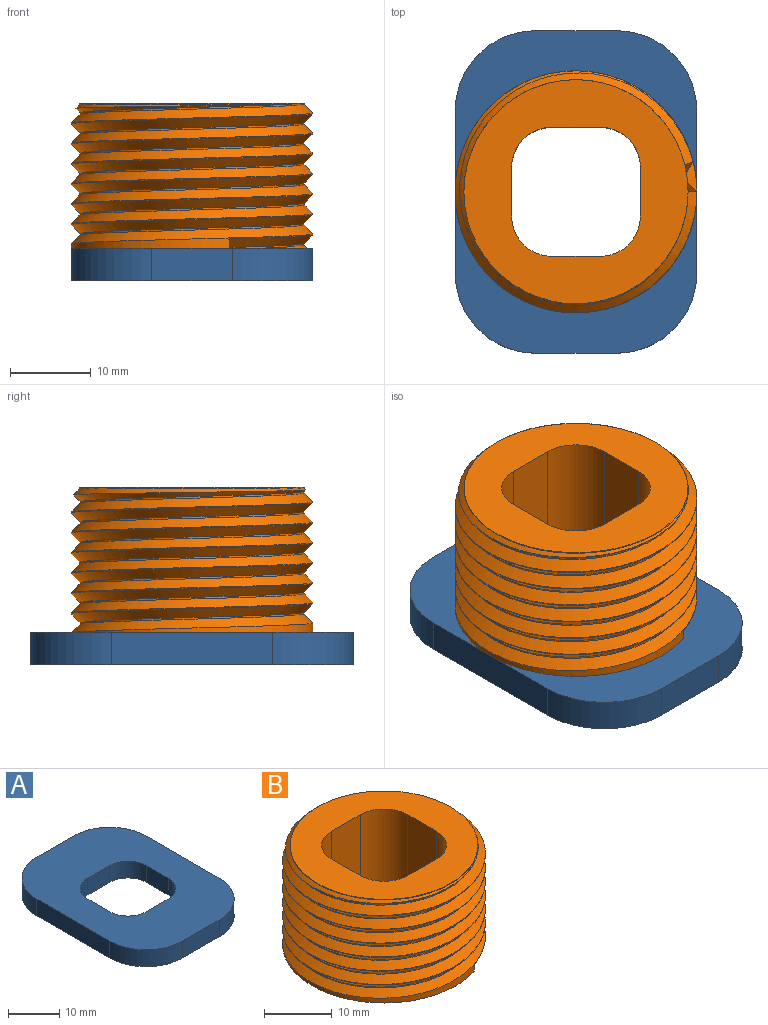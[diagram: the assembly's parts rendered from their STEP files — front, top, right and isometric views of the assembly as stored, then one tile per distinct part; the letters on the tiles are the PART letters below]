
ASSEMBLY  parts=2 mates=1
PART A: 18 faces, bbox 30x40x4 mm
  f0: plane 6x4mm, normal (1,0,0), area 24mm2, adj f4,f7,f8,f9
  f1: plane 6x4mm, normal (0,-1,0), area 24mm2, adj f4,f5,f8,f9
  f2: plane 6x4mm, normal (-1,0,0), area 24mm2, adj f5,f6,f8,f9
  f3: plane 6x4mm, normal (0,1,0), area 24mm2, adj f6,f7,f8,f9
  f4: cylinder r=5mm len=5mm, axis (0,0,-1), area 31.4mm2, adj f0,f1,f8,f9
  f5: cylinder r=5mm len=5mm, axis (0,0,1), area 31.4mm2, adj f1,f2,f8,f9
  f6: cylinder r=5mm len=5mm, axis (0,0,-1), area 31.4mm2, adj f2,f3,f8,f9
  f7: cylinder r=5mm len=5mm, axis (0,0,1), area 31.4mm2, adj f0,f3,f8,f9
  f8: plane 40x30mm, normal (0,0,1), area 879.6mm2, adj f0,f1,f2,f3,f4,f5,f6,f7
  f9: plane 40x30mm, normal (0,0,-1), area 879.6mm2, adj f0,f1,f2,f3,f4,f5,f6,f7
  f10: plane 20x4mm, normal (1,0,0), area 80mm2, adj f8,f9,f14,f17
  f11: plane 10x4mm, normal (0,1,0), area 40mm2, adj f8,f9,f14,f15
  f12: plane 20x4mm, normal (-1,0,0), area 80mm2, adj f8,f9,f15,f16
  f13: plane 10x4mm, normal (0,-1,0), area 40mm2, adj f8,f9,f16,f17
  f14: cylinder r=10mm len=10mm, axis (0,0,1), area 62.8mm2, adj f8,f9,f10,f11
  f15: cylinder r=10mm len=10mm, axis (0,0,-1), area 62.8mm2, adj f8,f9,f11,f12
  f16: cylinder r=10mm len=10mm, axis (0,0,1), area 62.8mm2, adj f8,f9,f12,f13
  f17: cylinder r=10mm len=10mm, axis (0,0,-1), area 62.8mm2, adj f8,f9,f10,f13
PART B: 17 faces, bbox 30.1x34.7x20.3 mm
  f0: cylinder r=15mm len=30mm, axis (0,0,-1), area -339.8mm2, adj f1,f3,f4,f6
  f1: bspline ~34.64x30.04mm, area 945.7mm2, adj f0,f4,f5,f16
  f2: plane 28.03x27.93mm, normal (0,0,1), area 372.5mm2, adj f5,f7,f8,f9,f10,f11,f12,f13
  f3: plane 29.98x29.35mm, normal (0,0,-1), area 446mm2, adj f0,f4,f5,f6,f7,f8,f9,f10
  f4: plane 1.21x1.06mm, normal (0.95,0.31,0.03), area 0.7mm2, adj f0,f1,f3,f5
  f5: bspline ~32.1x27.8mm, area 123.8mm2, adj f1,f2,f3,f4,f6,f15
  f6: bspline ~29.99x29.97mm, area 929.5mm2, adj f0,f3,f5,f16
  f7: plane 18x6mm, normal (0,-1,0), area 108mm2, adj f2,f3,f11,f14
  f8: plane 18x6mm, normal (1,0,0), area 108mm2, adj f2,f3,f11,f12
  f9: plane 18x6mm, normal (0,1,0), area 108mm2, adj f2,f3,f12,f13
  f10: plane 18x6mm, normal (-1,0,0), area 108mm2, adj f2,f3,f13,f14
  f11: cylinder r=5mm len=18mm, axis (0,0,1), area 141.4mm2, adj f2,f3,f7,f8
  f12: cylinder r=5mm len=18mm, axis (0,0,-1), area 141.4mm2, adj f2,f3,f8,f9
  f13: cylinder r=5mm len=18mm, axis (0,0,1), area 141.4mm2, adj f2,f3,f9,f10
  f14: cylinder r=5mm len=18mm, axis (0,0,-1), area 141.4mm2, adj f2,f3,f7,f10
  f15: revolved ~27.78x27.77mm, area 8.4mm2, adj f2,f5,f16
  f16: revolved ~29.98x29.96mm, area -66.6mm2, adj f1,f6,f15
PLACE A t=(15.73,35.19,-23.83)mm
PLACE B t=(15.73,35.19,30.17)mm
MATE fastened A.f8 <-> B.f0  axis (0,0,1) through (15.73,35.19,30.17)mm
